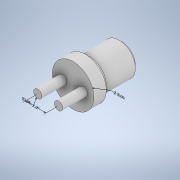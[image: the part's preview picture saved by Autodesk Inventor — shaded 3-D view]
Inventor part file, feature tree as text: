
AUTODESK INVENTOR PART (.ipt)
format: ipt  version: 2021 (Build 250183000, 183)  size: 131,072 bytes
history: native  units: mm
features: other x5, sketch x3, revolve x1, sweep x1
ambient origin geometry x8: Origin, YZ Plane, XZ Plane, XY Plane, X Axis, Y Axis, Z Axis, Center Point
bodies: Body1 (feature_tree)
feature tree (10):
  other  "Твердое тело1"
  other  "Аннотации"
  revolve  "Вращение1"
  sweep  "Сдвиг2"
  sketch  "Эскиз1"
  sketch  "Эскиз6"
  sketch  "3D эскиз3"
  other  "Диаметр 1"
  other  "Диаметр 2"
  other  "Линейный размер 1"
